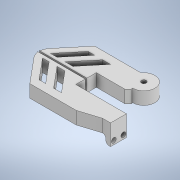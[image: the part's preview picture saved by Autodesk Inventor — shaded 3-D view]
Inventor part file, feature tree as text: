
AUTODESK INVENTOR PART (.ipt)
format: ipt  version: 2021 (Build 250183000, 183)  size: 229,888 bytes
history: native  units: mm
features: extrude x8, sketch x8, other x1, fillet x1, chamfer x1
ambient origin geometry x8: Origin, YZ Plane, XZ Plane, XY Plane, X Axis, Y Axis, Z Axis, Center Point
bodies: Body1 (feature_tree)
feature tree (19):
  other  "Sólido1"
  extrude  "Extrusión1"  Depth=6.0mm
  extrude  "Extrusión2"  Depth=8.0mm TaperAngle=0.0deg
  extrude  "Extrusión3"  Depth=4.0mm TaperAngle=0.0deg
  extrude  "Extrusión4"  Depth=8.0mm TaperAngle=0.0deg
  extrude  "Extrusión5"  Depth=2.0mm
  extrude  "Extrusión6"  Depth=2.0mm
  extrude  "Extrusión7"  Depth=3.0mm TaperAngle=0.0deg
  extrude  "Extrusión8"  Depth=2.0mm TaperAngle=0.0deg
  fillet  "Empalme1"  Radius=5.0mm
  chamfer  "Chaflán1"  Distance=5.0mm
  sketch  "Boceto1"  dims[d1=6.0mm d8=6.0mm]
  sketch  "Boceto2"  dims[d9=0.5mm d10=8.0mm d11=0.0mm]
  sketch  "Boceto3"  dims[d12=6.0mm d13=4.0mm d14=0.0mm]
  sketch  "Boceto4"  dims[d15=5.0mm d16=8.0mm d17=0.0mm]
  sketch  "Boceto5"  dims[d18=5.0mm d19=2.0mm]
  sketch  "Boceto6"  dims[d20=2.0mm d21=3.0mm]
  sketch  "Boceto7"  dims[d22=3.0mm d23=3.0mm d24=0.0mm]
  sketch  "Boceto8"  dims[d25=3.0mm d26=5.0mm d27=0.0mm d28=5.0mm d29=5.0mm d30=5.0mm d31=5.0mm d32=5.0mm d33=5.0mm d34=5.0mm d35=5.0mm d36=5.0mm d37=10.0mm d38=0.0mm d39=10.0mm d40=0.0mm d41=8.0mm d42=0.0mm d43=2.0mm d44=2.0mm d45=2.0mm d46=45.0deg]
